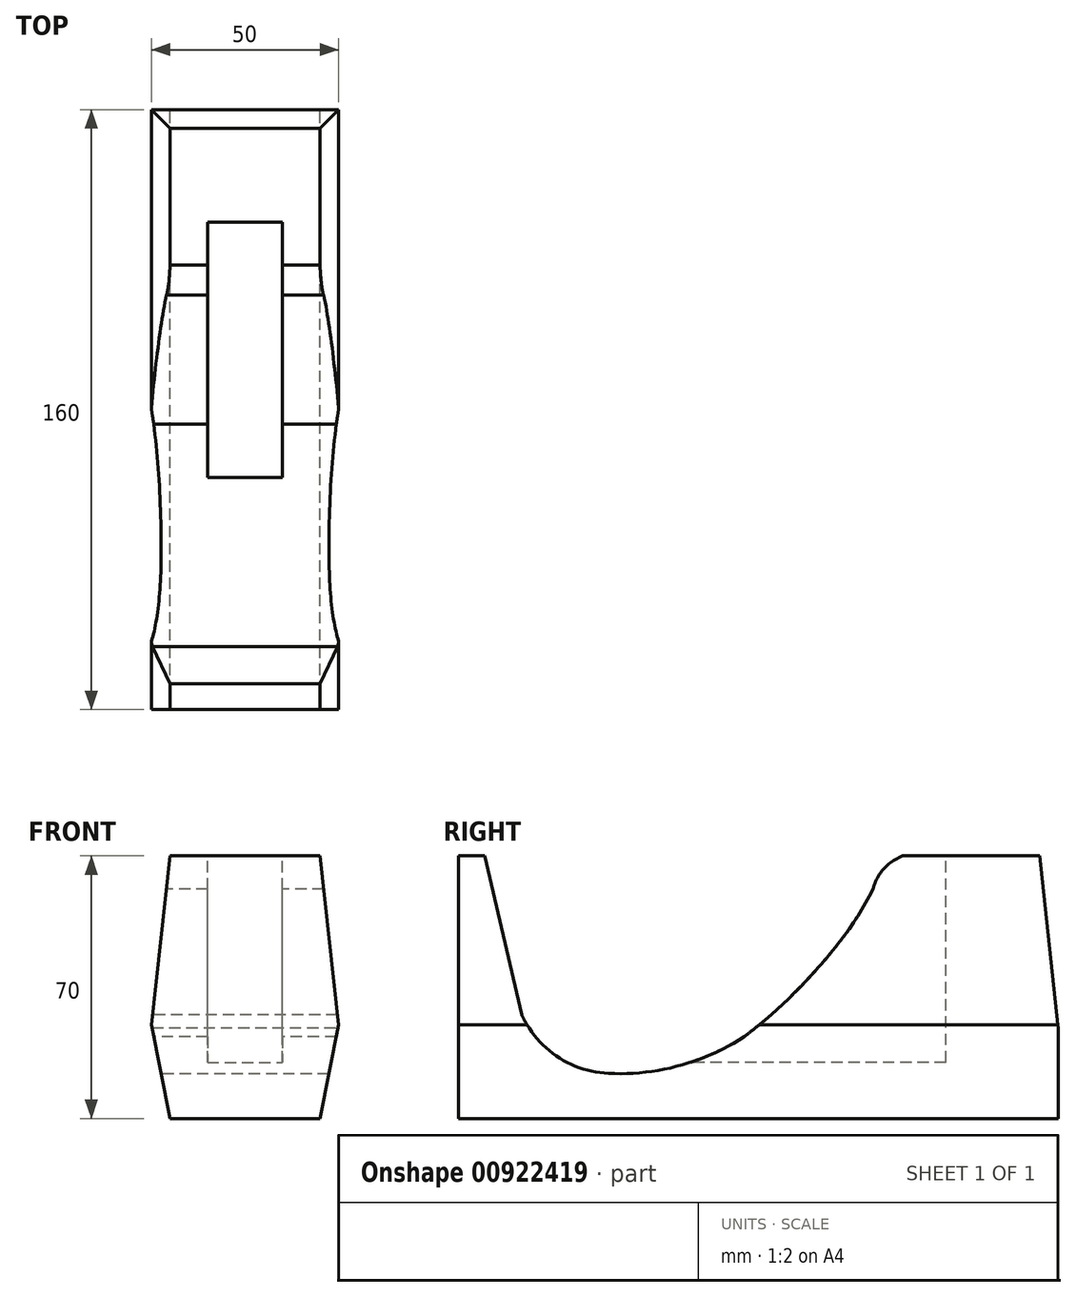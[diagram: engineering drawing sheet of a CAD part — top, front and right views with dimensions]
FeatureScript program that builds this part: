
annotation { "Feature Type Name" : "Feature", "Feature Type Description" : "" }
export const myFeature = defineFeature(function(context is Context, id is Id, definition is map)
    precondition{}
    {
        {
            var Q0;
            Q0=qCreatedBy(makeId("Front.planeOp"),FACE);
            var sketch = newSketch(context, id + "F0", { "sketchPlane" : qUnion([Q0])});
            skLineSegment(sketch, "E0.bottom", {"start": v(-16.2, 70) * mm, "end": v(23.8, 70) * mm});
            skLineSegment(sketch, "E0.top", {"start": v(-16.2, 0) * mm, "end": v(23.8, 0) * mm});
            skLineSegment(sketch, "E1.top", {"start": v(-16.2, 25) * mm, "end": v(23.8, 25) * mm});
            skLineSegment(sketch, "E2", {"start": v(-16.2, 70) * mm, "end": v(-21.2, 25) * mm});
            skLineSegment(sketch, "E3", {"start": v(-21.2, 25) * mm, "end": v(-16.2, 0) * mm});
            skLineSegment(sketch, "E4", {"start": v(23.8, 0) * mm, "end": v(28.8, 25) * mm});
            skLineSegment(sketch, "E5", {"start": v(28.8, 25) * mm, "end": v(23.8, 70) * mm});
            skPoint(sketch, "E6.orphan", {"position": v(28.8, 0) * mm});
            skLineSegment(sketch, "E7.top", {"start": v(-21.2, 70) * mm, "end": v(-16.2, 70) * mm});
            skLineSegment(sketch, "E7.left", {"start": v(-21.2, 25) * mm, "end": v(-21.2, 70) * mm});
            skLineSegment(sketch, "E8.top", {"start": v(28.8, 70) * mm, "end": v(23.8, 70) * mm});
            skLineSegment(sketch, "E8.left", {"start": v(28.8, 25) * mm, "end": v(28.8, 70) * mm});
            skLineSegment(sketch, "E9.top", {"start": v(-21.2, 0) * mm, "end": v(-16.2, 0) * mm});
            skLineSegment(sketch, "E9.left", {"start": v(-21.2, 25) * mm, "end": v(-21.2, 0) * mm});
            skLineSegment(sketch, "E10.top", {"start": v(28.8, 0) * mm, "end": v(23.8, 0) * mm});
            skLineSegment(sketch, "E10.left", {"start": v(28.8, 25) * mm, "end": v(28.8, 0) * mm});
            skSolve(sketch);
        }
        {
            var Q0;
            Q0=makeQuery(id+"F0.imprint","IMPRINT",FACE,{"disambiguationData":[TD([[makeQuery(id+"F0.imprint","IMPRINT",EDGE,{"derivedFrom":sQuery(id+"F0.wireOp",EDGE,"E2")}),-1.0]])]});
            var Q1;
            Q1=makeQuery(id+"F0.imprint","IMPRINT",FACE,{"disambiguationData":[TD([[makeQuery(id+"F0.imprint","IMPRINT",EDGE,{"derivedFrom":sQuery(id+"F0.wireOp",EDGE,"E0.bottom")}),-1.0]])]});
            var Q2;
            Q2=makeQuery(id+"F0.imprint","IMPRINT",FACE,{"disambiguationData":[TD([[makeQuery(id+"F0.imprint","IMPRINT",EDGE,{"derivedFrom":sQuery(id+"F0.wireOp",EDGE,"E5")}),-1.0]])]});
            var Q3;
            Q3=makeQuery(id+"F0.imprint","IMPRINT",FACE,{"disambiguationData":[TD([[makeQuery(id+"F0.imprint","IMPRINT",EDGE,{"derivedFrom":sQuery(id+"F0.wireOp",EDGE,"E4")}),-1.0]])]});
            var Q4;
            Q4=makeQuery(id+"F0.imprint","IMPRINT",FACE,{"disambiguationData":[TD([[makeQuery(id+"F0.imprint","IMPRINT",EDGE,{"derivedFrom":sQuery(id+"F0.wireOp",EDGE,"E3")}),-1.0]])]});
            extrude(context, id + "F1", {"entities" : qUnion([Q0, Q1, Q2, Q3, Q4]), "depth" : 160 * mm, "offsetDistance" : 25 * mm});
        }
        {
            var Q0;
            Q0=makeQuery(id+"F1.opExtrude","SWEPT_FACE",FACE,{"disambiguationData":[OSD([sQuery(id+"F0.wireOp",EDGE,"E8.left"),sQuery(id+"F0.wireOp",EDGE,"E10.left")])]});
            var sketch = newSketch(context, id + "F2", { "sketchPlane" : qUnion([Q0])});
            skLineSegment(sketch, "E11.bottom", {"start": v(0, 0) * mm, "end": v(-160, 0) * mm});
            skLineSegment(sketch, "E11.left", {"start": v(0, 0) * mm, "end": v(0, 24.21) * mm});
            skLineSegment(sketch, "E11.right", {"start": v(-160, 0) * mm, "end": v(-160, 24.21) * mm});
            skLineSegment(sketch, "E12.top", {"start": v(0, 70) * mm, "end": v(-5, 70) * mm});
            skLineSegment(sketch, "E12.left", {"start": v(0, 24.21) * mm, "end": v(0, 70) * mm});
            skLineSegment(sketch, "E13.top", {"start": v(-5, 0) * mm, "end": v(0, 0) * mm});
            skLineSegment(sketch, "E13.right", {"start": v(0, 24.21) * mm, "end": v(0, 0) * mm});
            skLineSegment(sketch, "E14.bottom", {"start": v(-160, 0) * mm, "end": v(-150, 0) * mm});
            skLineSegment(sketch, "E14.left", {"start": v(-160, 0) * mm, "end": v(-160, 70) * mm});
            skLineSegment(sketch, "E15", {"start": v(0, 24.21) * mm, "end": v(-5, 70) * mm});
            skLineSegment(sketch, "E16", {"start": v(0, 24.21) * mm, "end": v(-5, 0) * mm});
            skLineSegment(sketch, "E17", {"start": v(-150, 0) * mm, "end": v(-160, 70) * mm});
            skSolve(sketch);
        }
        {
            var Q0;
            Q0=makeQuery(id+"F1.opExtrude","SWEPT_FACE",FACE,{"disambiguationData":[OSD([sQuery(id+"F0.wireOp",EDGE,"E0.bottom"),sQuery(id+"F0.wireOp",EDGE,"E7.top"),sQuery(id+"F0.wireOp",EDGE,"E8.top")])]});
            var sketch = newSketch(context, id + "F3", { "sketchPlane" : qUnion([Q0])});
            skLineSegment(sketch, "E18.top", {"start": v(-6.2, -30) * mm, "end": v(13.8, -30) * mm});
            skLineSegment(sketch, "E19.right", {"start": v(-6.2, -30) * mm, "end": v(-6.2, -105) * mm});
            skLineSegment(sketch, "E20.right", {"start": v(13.8, -30) * mm, "end": v(13.8, -105) * mm});
            skLineSegment(sketch, "E21.bottom", {"start": v(13.8, -105) * mm, "end": v(-6.2, -105) * mm});
            skLineSegment(sketch, "E21.top", {"start": v(13.8, -30) * mm, "end": v(-6.2, -30) * mm});
            skLineSegment(sketch, "E21.left", {"start": v(13.8, -105) * mm, "end": v(13.8, -30) * mm});
            skLineSegment(sketch, "E21.right", {"start": v(-6.2, -105) * mm, "end": v(-6.2, -30) * mm});
            skSolve(sketch);
        }
        {
            var Q0;
            Q0=makeQuery(id+"F3.imprint","IMPRINT",FACE,{"disambiguationData":[TD([[makeQuery(id+"F3.imprint","IMPRINT",EDGE,{"derivedFrom":sQuery(id+"F3.wireOp",EDGE,"E21.bottom")}),-1.0]])]});
            extrude(context, id + "F4", {"entities" : qUnion([Q0]), "operationType" : NewBodyOperationType.REMOVE, "oppositeDirection" : true, "depth" : 55 * mm, "offsetDistance" : 25 * mm});
        }
        {
            var Q0;
            Q0=makeQuery(id+"F1.opExtrude","SWEPT_FACE",FACE,{"disambiguationData":[OSD([sQuery(id+"F0.wireOp",EDGE,"E7.left"),sQuery(id+"F0.wireOp",EDGE,"E9.left")])]});
            var sketch = newSketch(context, id + "F5", { "sketchPlane" : qUnion([Q0])});
            skLineSegment(sketch, "E22.bottom", {"start": v(160, 0) * mm, "end": v(120, 0) * mm});
            skLineSegment(sketch, "E22.top", {"start": v(160, 37) * mm, "end": v(120, 37) * mm});
            skLineSegment(sketch, "E22.left", {"start": v(160, 0) * mm, "end": v(160, 37) * mm});
            skLineSegment(sketch, "E22.right", {"start": v(120, 0) * mm, "end": v(120, 37) * mm});
            skLineSegment(sketch, "E23", {"start": v(143.2, 27.68) * mm, "end": v(153.08, 70) * mm});
            skArc(sketch, "E24", {"start": v(83.87, 21.77) * mm, "mid": v(101.17, 14.07) * mm, "end": v(120, 12) * mm});
            skPoint(sketch, "E24.endSnap0", {"position": v(120, 18.5) * mm});
            skFitSpline(sketch, "E25", {"points": [v(83.87, 21.77) * mm, v(74.1, 29.91) * mm, v(56.6, 49.45) * mm, v(46.82, 66.3) * mm], "startDerivative": vector(-32.94, 25.45) * mm, "endDerivative": vector(-23.82, 48.79) * mm});
            skArc(sketch, "E26", {"start": v(49.5, 60.82) * mm, "mid": v(46.7, 66.44) * mm, "end": v(41.53, 70) * mm});
            skArc(sketch, "E27", {"start": v(120, 12) * mm, "mid": v(133.82, 16.55) * mm, "end": v(143.2, 27.68) * mm});
            skSolve(sketch);
        }
        {
            var Q0;
            {var subQ5=sQuery(id+"F5.wireOp",EDGE,"E27");Q0=makeQuery(id+"F5.imprint","IMPRINT",FACE,{"disambiguationData":[TD([[makeQuery(id+"F5.imprint","IMPRINT",EDGE,{"derivedFrom":subQ5}),1.0]])]});}
            var Q1;
            {var subQ0=sQuery(id+"F5.wireOp",EDGE,"E24");Q1=makeQuery(id+"F5.imprint","IMPRINT",FACE,{"disambiguationData":[TD([[makeQuery(id+"F5.imprint","IMPRINT",EDGE,{"derivedFrom":subQ0}),1.0]])]});}
            extrude(context, id + "F6", {"entities" : qUnion([Q0, Q1]), "operationType" : NewBodyOperationType.REMOVE, "oppositeDirection" : true, "depth" : 80 * mm, "offsetDistance" : 25 * mm});
        }
        {
            var Q0;
            {var subQ0=sQuery(id+"F2.wireOp",EDGE,"E14.bottom");Q0=makeQuery(id+"F2.imprint","IMPRINT",FACE,{"disambiguationData":[TD([[makeQuery(id+"F2.imprint","IMPRINT",EDGE,{"derivedFrom":subQ0}),1.0]])]});}
            var Q1;
            Q1=makeQuery(id+"F2.imprint","IMPRINT",FACE,{"disambiguationData":[TD([[makeQuery(id+"F2.imprint","IMPRINT",EDGE,{"derivedFrom":sQuery(id+"F2.wireOp",EDGE,"E12.top")}),-1.0]])]});
            var Q2;
            Q2=makeQuery(id+"F2.imprint","IMPRINT",FACE,{"disambiguationData":[TD([[makeQuery(id+"F2.imprint","IMPRINT",EDGE,{"derivedFrom":sQuery(id+"F2.wireOp",EDGE,"E13.top")}),1.0]])]});
            extrude(context, id + "F7", {"entities" : qUnion([Q0, Q1, Q2]), "operationType" : NewBodyOperationType.REMOVE, "oppositeDirection" : true, "depth" : 80 * mm, "offsetDistance" : 25 * mm});
        }
        {
            var Q0;
            Q0=makeQuery(id+"F0.imprint","IMPRINT",FACE,{"disambiguationData":[TD([[makeQuery(id+"F0.imprint","IMPRINT",EDGE,{"derivedFrom":sQuery(id+"F0.wireOp",EDGE,"E5")}),-1.0]])]});
            var Q1;
            Q1=makeQuery(id+"F0.imprint","IMPRINT",FACE,{"disambiguationData":[TD([[makeQuery(id+"F0.imprint","IMPRINT",EDGE,{"derivedFrom":sQuery(id+"F0.wireOp",EDGE,"E2")}),-1.0]])]});
            var Q2;
            Q2=makeQuery(id+"F0.imprint","IMPRINT",FACE,{"disambiguationData":[TD([[makeQuery(id+"F0.imprint","IMPRINT",EDGE,{"derivedFrom":sQuery(id+"F0.wireOp",EDGE,"E4")}),-1.0]])]});
            var Q3;
            Q3=makeQuery(id+"F0.imprint","IMPRINT",FACE,{"disambiguationData":[TD([[makeQuery(id+"F0.imprint","IMPRINT",EDGE,{"derivedFrom":sQuery(id+"F0.wireOp",EDGE,"E3")}),-1.0]])]});
            extrude(context, id + "F8", {"entities" : qUnion([Q0, Q1, Q2, Q3]), "operationType" : NewBodyOperationType.REMOVE, "depth" : 200 * mm, "offsetDistance" : 25 * mm});
        }
    });
